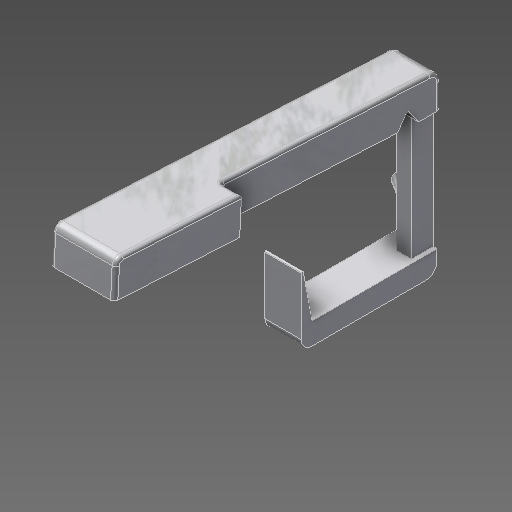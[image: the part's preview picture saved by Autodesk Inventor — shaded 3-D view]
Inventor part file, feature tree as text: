
AUTODESK INVENTOR PART (.ipt)
format: ipt  version: 2020 (Build 240168000, 168)  size: 327,168 bytes
history: native  units: mm
features: extrude x7, fillet x6, other x3, draft x1, chamfer x1
ambient origin geometry x8: Origin, YZ Plane, XZ Plane, XY Plane, X Axis, Y Axis, Z Axis, Center Point
bodies: Solid1 (feature_tree)
feature tree (18):
  other  "Key Sketch"
  extrude  "Upper Key"  Depth=10.0mm
  extrude  "Lower Key"  Depth=1.0mm
  other  "Hinge Cut Sketch"
  extrude  "Hinge Cut"  Depth=10.0mm TaperAngle=0.0deg
  extrude  "Hinge Cut 2"  Depth=3.0mm
  other  "Lever Sketch"
  extrude  "Vertical Lever"  Depth=3.0mm
  extrude  "Horizontal Lever"  Depth=33.6625mm
  extrude  "Spring Hook"  Depth=0.5mm
  draft  "FaceDraft3"
  chamfer  "Chamfer1"  Distance=3.0mm
  fillet  "Fillet9"  Radius=6.0mm
  fillet  "Fillet10"  Radius=4.0mm
  fillet  "Fillet5"  Radius=10.0mm
  fillet  "Fillet4"  [1 undecoded]
  fillet  "Fillet11"  Radius=3.0mm
  fillet  "Fillet14"  Radius=2.3mm
note: 1 required parameter value undecoded (feature->parameter linkage not recoverable at this tier; creation-order binding heuristic only, values carry confidence <= 0.55)
